# Revit family: Shower-Haws_Corporation-Combination_Unit_8330
name_source: partatom
category: Plumbing Fixtures
revit_build: Autodesk Revit 2015 (Build: 20140606_1530(x64)
units: mm (PartAtom-declared; Revit-internal decimal feet)

## types (1)
- Axion MSR - Combination Unit 8330
    Assembly Code = D2010710
    BIMobject category = Other
    BIMobject category code = sanitary-sanitary-other
    BIMobject main category = Sanitary
    BIMobject main category code = sanitary
    Bowl = Metal - Haws Corporation - High Polished Stainless Steel
    Brand url = https://www.hawsco.com
    CW Connection = Yes
    CWFU = 1
    Cost = 0 $
    Cost Note = For Cost information please visit the Resource tab in the Product Page URL
    Date of publishing = 7/31/2014
    Description = Traditional eyewashes irrigate from the outside edge of the eye back toward the nose
    Design country = United States
    EAN code = https://611970353210
    Edition number = 1
    Eye face wash head = 41 3/4"
    Flow = 20 GPM
    Full Height = 89 1/4"
    HW Connection = No
    HWFU = 1
    Installation instructions = http://www.hawsco.com
    Keynote = 15410
    Lever Height = 65 3/8"
    Manufacturer = Haws Corporation
    Manufacturer country = United States
    Manufacturer name = Haws Corporation
    Masterformat 2014 Code = 22 45 26
    Masterformat 2014 Description = Eye/Face Wash Equipment
    Material main = Metal
    Model = 8330
    Nominal height = 91"
    Nominal width = 15"
    OmniClass Code = 23-29 37 13 15
    OmniClass Description = Combination Emergency Eye Wash Stations
    Product Documentation Link = https://www.hawsco.com
    Product Guid = 8dfc0aa1-c186-40e7-a12f-b63985dac2b5
    Product Page URL = http://www.hawsco.com
    Product SKU = haws-8330
    Product certification = http://www.csagroup.org
    Product data url = https://bimobject.com
    Product family = Eye Wash Fountains
    Product group = Emergency Equipment - Eye & Face Washes
    Product url = https://www.hawsco.com
    Pull Rod = Metal - Haws Corporation - High Polished Stainless Steel
    QR code = http://bimobject.com
    Sanitary Radius = 5/8"
    Series = AXION MSR™
    Shower Arm Overhang = 25"
    Shower Head = Metal - Haws Corporation - High Polished Stainless Steel
    Supply Radius = 5/8"
    Technical description = http://www.hawsco.com
    Tubing = Metal - Haws Corporation - Galvanized Steel
    Type Comments = Combination shower and eyewash features the medically acclaimed AXION MSR™ eye/face wash head assembly
    UNSPSC Code = 46182402
    URL = http://www.hawsco.com
    Vent Connection = No
    Version = 2014-v2.0a
    WFU = 1
    Waste Connection = Yes
    Weight Net (Kg) = 52

## geometry (parser evidence)
native form markers: Blend x16, Sweep x9
no freeform markers — native parametric forms only
